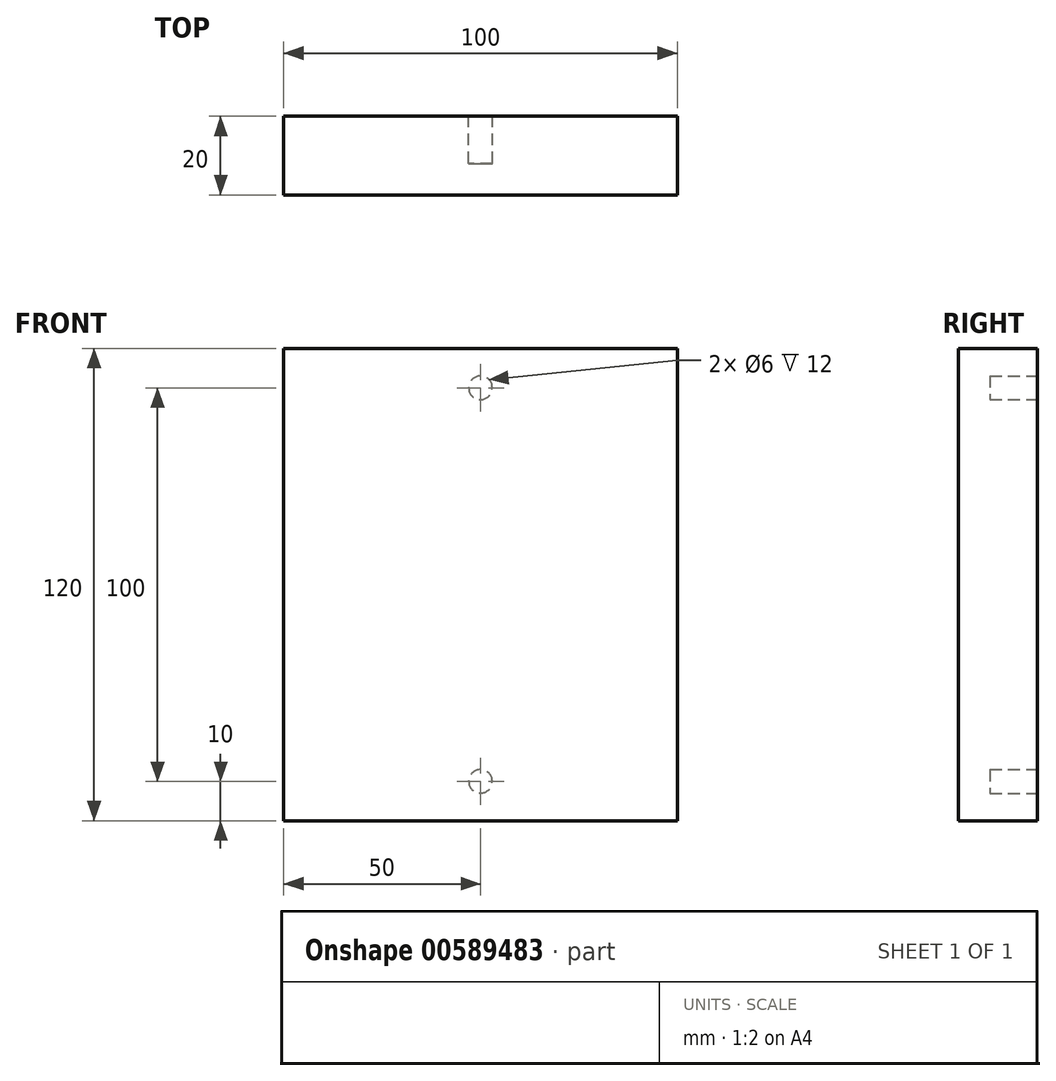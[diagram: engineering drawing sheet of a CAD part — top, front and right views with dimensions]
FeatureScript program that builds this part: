
annotation { "Feature Type Name" : "Feature", "Feature Type Description" : "" }
export const myFeature = defineFeature(function(context is Context, id is Id, definition is map)
    precondition{}
    {
        {
            var Q0;
            Q0=qCreatedBy(makeId("Top.planeOp"),FACE);
            var sketch = newSketch(context, id + "F0", { "sketchPlane" : qUnion([Q0])});
            skLineSegment(sketch, "E0.bottom", {"start": v(0, 0) * mm, "end": v(100, 0) * mm});
            skLineSegment(sketch, "E0.top", {"start": v(0, 20) * mm, "end": v(100, 20) * mm});
            skLineSegment(sketch, "E0.left", {"start": v(0, 0) * mm, "end": v(0, 20) * mm});
            skLineSegment(sketch, "E0.right", {"start": v(100, 0) * mm, "end": v(100, 20) * mm});
            skSolve(sketch);
        }
        {
            var Q0;
            Q0=makeQuery(id+"F0.imprint","IMPRINT",FACE,{"disambiguationData":[TD([[makeQuery(id+"F0.imprint","IMPRINT",EDGE,{"derivedFrom":sQuery(id+"F0.wireOp",EDGE,"E0.bottom")}),1.0]])]});
            extrude(context, id + "F1", {"entities" : qUnion([Q0]), "depth" : 120 * mm, "offsetDistance" : 25 * mm});
        }
        {
            var Q0;
            Q0=makeQuery(id+"F1.opExtrude","SWEPT_FACE",FACE,{"disambiguationData":[OSD([sQuery(id+"F0.wireOp",EDGE,"E0.top")])]});
            var sketch = newSketch(context, id + "F2", { "sketchPlane" : qUnion([Q0])});
            skCircle(sketch, "E1", {"center": v(-50, 110) * mm, "radius": 3 * mm});
            skPoint(sketch, "E1.centerSnap0", {"position": v(-50, 120) * mm});
            skSolve(sketch);
        }
        {
            var Q0;
            Q0=makeQuery(id+"F2.imprint","IMPRINT",FACE,{"disambiguationData":[TD([[makeQuery(id+"F2.imprint","IMPRINT",EDGE,{"derivedFrom":sQuery(id+"F2.wireOp",EDGE,"E1")}),1.0]])]});
            extrude(context, id + "F3", {"entities" : qUnion([Q0]), "operationType" : NewBodyOperationType.REMOVE, "oppositeDirection" : true, "depth" : 12 * mm, "offsetDistance" : 25 * mm});
        }
        {
            var Q0;
            Q0=makeQuery(id+"F1.opExtrude","SWEPT_FACE",FACE,{"disambiguationData":[OSD([sQuery(id+"F0.wireOp",EDGE,"E0.top")])]});
            var sketch = newSketch(context, id + "F4", { "sketchPlane" : qUnion([Q0])});
            skCircle(sketch, "E2", {"center": v(-50, 10) * mm, "radius": 3 * mm});
            skPoint(sketch, "E2.centerSnap0", {"position": v(-50, 120) * mm});
            skSolve(sketch);
        }
        {
            var Q0;
            Q0=makeQuery(id+"F4.imprint","IMPRINT",FACE,{"disambiguationData":[TD([[makeQuery(id+"F4.imprint","IMPRINT",EDGE,{"derivedFrom":sQuery(id+"F4.wireOp",EDGE,"E2")}),1.0]])]});
            extrude(context, id + "F5", {"entities" : qUnion([Q0]), "operationType" : NewBodyOperationType.REMOVE, "oppositeDirection" : true, "depth" : 12 * mm, "offsetDistance" : 25 * mm});
        }
    });
